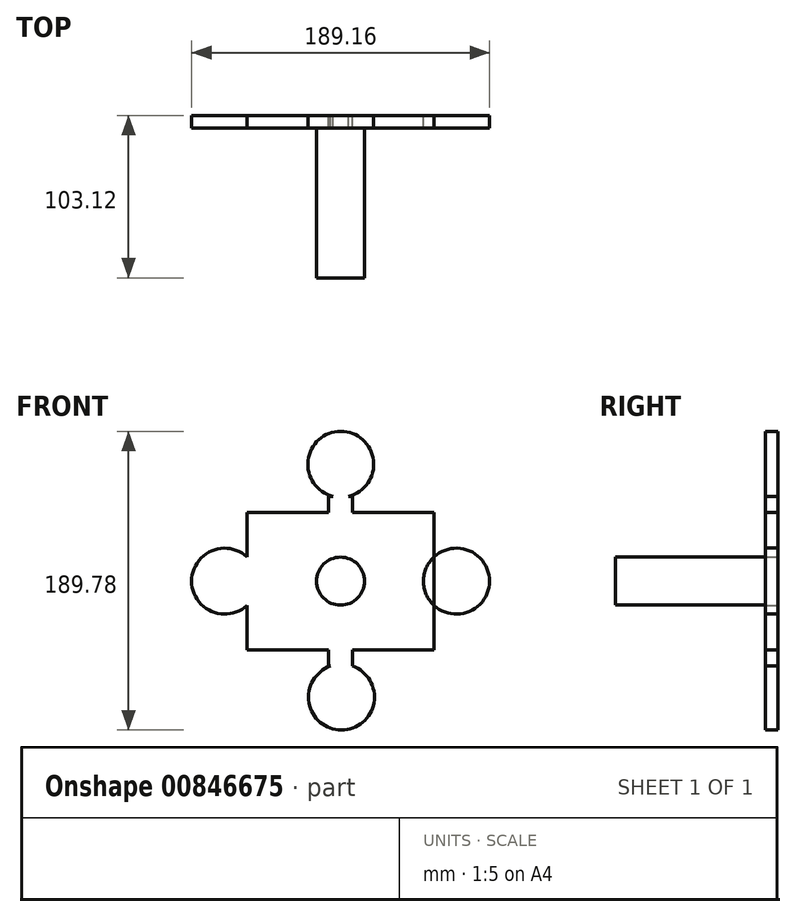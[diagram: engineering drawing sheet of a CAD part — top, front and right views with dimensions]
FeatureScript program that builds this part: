
annotation { "Feature Type Name" : "Feature", "Feature Type Description" : "" }
export const myFeature = defineFeature(function(context is Context, id is Id, definition is map)
    precondition{}
    {
        {
            var Q0;
            Q0=qCreatedBy(makeId("Front.planeOp"),FACE);
            var sketch = newSketch(context, id + "F0", { "sketchPlane" : qUnion([Q0])});
            skCircle(sketch, "E0", {"center": v(0, 0) * mm, "radius": 73.64 * mm, "construction": true});
            skCircle(sketch, "E1", {"center": v(-73.64, 0) * mm, "radius": 20.94 * mm});
            skCircle(sketch, "E2.MirrorC", {"center": v(73.64, 0) * mm, "radius": 20.94 * mm});
            skCircle(sketch, "E3", {"center": v(0.12, 74.26) * mm, "radius": 20.94 * mm});
            skCircle(sketch, "E4", {"center": v(0.6, -73.64) * mm, "radius": 20.94 * mm});
            skLineSegment(sketch, "E5.bottom", {"start": v(7.57, -53.9) * mm, "end": v(-7.57, -53.9) * mm});
            skLineSegment(sketch, "E5.top", {"start": v(7.57, 53.9) * mm, "end": v(-7.57, 53.9) * mm});
            skLineSegment(sketch, "E5.left", {"start": v(7.57, -53.9) * mm, "end": v(7.57, 53.9) * mm});
            skLineSegment(sketch, "E5.right", {"start": v(-7.57, -53.9) * mm, "end": v(-7.57, 53.9) * mm});
            skLineSegment(sketch, "E6.bottom", {"start": v(59.32, -43.64) * mm, "end": v(-59.32, -43.64) * mm});
            skLineSegment(sketch, "E6.top", {"start": v(59.32, 43.64) * mm, "end": v(-59.32, 43.64) * mm});
            skLineSegment(sketch, "E6.left", {"start": v(59.32, -43.64) * mm, "end": v(59.32, 43.64) * mm});
            skLineSegment(sketch, "E6.right", {"start": v(-59.32, -43.64) * mm, "end": v(-59.32, 43.64) * mm});
            skSolve(sketch);
        }
        {
            var Q0;
            {var subQ0=sQuery(id+"F0.wireOp",EDGE,"E5.top");var subQ1=sQuery(id+"F0.wireOp",EDGE,"E3");var subQ2=makeQuery(id+"F0.imprint","INTERSECT",VERTEX,{"disambiguationData":[OD(0.0)],"derivedFrom":[subQ1,subQ0]});Q0=makeQuery(id+"F0.imprint","IMPRINT",FACE,{"disambiguationData":[TD([[makeQuery(id+"F0.imprint","IMPRINT",EDGE,{"disambiguationData":[TD([[subQ2,-1.0]])],"derivedFrom":subQ1}),1.0]])]});}
            var Q1;
            {var subQ0=sQuery(id+"F0.wireOp",EDGE,"E6.right");var subQ8=sQuery(id+"F0.wireOp",EDGE,"E1");var subQ9=makeQuery(id+"F0.imprint","INTERSECT",VERTEX,{"disambiguationData":[OD(0.0)],"derivedFrom":[subQ8,subQ0]});Q1=makeQuery(id+"F0.imprint","IMPRINT",FACE,{"disambiguationData":[TD([[makeQuery(id+"F0.imprint","IMPRINT",EDGE,{"disambiguationData":[TD([[subQ9,-1.0]])],"derivedFrom":subQ8}),-1.0]])]});}
            var Q2;
            {var subQ0=sQuery(id+"F0.wireOp",EDGE,"E6.bottom");var subQ1=sQuery(id+"F0.wireOp",EDGE,"E5.left");var subQ2=makeQuery(id+"F0.imprint","INTERSECT",VERTEX,{"derivedFrom":[subQ1,subQ0]});Q2=makeQuery(id+"F0.imprint","IMPRINT",FACE,{"disambiguationData":[TD([[makeQuery(id+"F0.imprint","IMPRINT",EDGE,{"disambiguationData":[TD([[subQ2,-1.0]])],"derivedFrom":subQ1}),1.0]])]});}
            var Q3;
            {var subQ0=sQuery(id+"F0.wireOp",EDGE,"E6.left");var subQ8=sQuery(id+"F0.wireOp",EDGE,"E2.MirrorC");var subQ9=makeQuery(id+"F0.imprint","INTERSECT",VERTEX,{"disambiguationData":[OD(0.0)],"derivedFrom":[subQ8,subQ0]});Q3=makeQuery(id+"F0.imprint","IMPRINT",FACE,{"disambiguationData":[TD([[makeQuery(id+"F0.imprint","IMPRINT",EDGE,{"disambiguationData":[TD([[subQ9,-1.0]])],"derivedFrom":subQ8}),1.0]])]});}
            var Q4;
            {var subQ1=sQuery(id+"F0.wireOp",EDGE,"E5.top");var subQ3=sQuery(id+"F0.wireOp",EDGE,"E3");var subQ10=makeQuery(id+"F0.imprint","INTERSECT",VERTEX,{"disambiguationData":[OD(0.0)],"derivedFrom":[subQ3,subQ1]});Q4=makeQuery(id+"F0.imprint","IMPRINT",FACE,{"disambiguationData":[TD([[makeQuery(id+"F0.imprint","IMPRINT",EDGE,{"disambiguationData":[TD([[subQ10,1.0]])],"derivedFrom":subQ3}),-1.0]])]});}
            var Q5;
            {var subQ0=sQuery(id+"F0.wireOp",EDGE,"E6.left");var subQ1=sQuery(id+"F0.wireOp",EDGE,"E2.MirrorC");var subQ2=makeQuery(id+"F0.imprint","INTERSECT",VERTEX,{"disambiguationData":[OD(0.0)],"derivedFrom":[subQ1,subQ0]});Q5=makeQuery(id+"F0.imprint","IMPRINT",FACE,{"disambiguationData":[TD([[makeQuery(id+"F0.imprint","IMPRINT",EDGE,{"disambiguationData":[TD([[subQ2,-1.0]])],"derivedFrom":subQ1}),-1.0]])]});}
            var Q6;
            {var subQ0=sQuery(id+"F0.wireOp",EDGE,"E6.right");var subQ1=sQuery(id+"F0.wireOp",EDGE,"E1");var subQ2=makeQuery(id+"F0.imprint","INTERSECT",VERTEX,{"disambiguationData":[OD(0.0)],"derivedFrom":[subQ1,subQ0]});Q6=makeQuery(id+"F0.imprint","IMPRINT",FACE,{"disambiguationData":[TD([[makeQuery(id+"F0.imprint","IMPRINT",EDGE,{"disambiguationData":[TD([[subQ2,1.0]])],"derivedFrom":subQ1}),1.0]])]});}
            var Q7;
            {var subQ0=sQuery(id+"F0.wireOp",EDGE,"E6.right");var subQ1=sQuery(id+"F0.wireOp",EDGE,"E1");var subQ2=makeQuery(id+"F0.imprint","INTERSECT",VERTEX,{"disambiguationData":[OD(0.0)],"derivedFrom":[subQ1,subQ0]});Q7=makeQuery(id+"F0.imprint","IMPRINT",FACE,{"disambiguationData":[TD([[makeQuery(id+"F0.imprint","IMPRINT",EDGE,{"disambiguationData":[TD([[subQ2,-1.0]])],"derivedFrom":subQ1}),1.0]])]});}
            var Q8;
            {var subQ0=sQuery(id+"F0.wireOp",EDGE,"E5.bottom");var subQ1=sQuery(id+"F0.wireOp",EDGE,"E4");var subQ3=makeQuery(id+"F0.imprint","INTERSECT",VERTEX,{"derivedFrom":[subQ1,subQ0]});Q8=makeQuery(id+"F0.imprint","IMPRINT",FACE,{"disambiguationData":[TD([[makeQuery(id+"F0.imprint","IMPRINT",EDGE,{"disambiguationData":[TD([[subQ3,-1.0]])],"derivedFrom":subQ1}),1.0]])]});}
            var Q9;
            {var subQ1=sQuery(id+"F0.wireOp",EDGE,"E5.bottom");var subQ6=sQuery(id+"F0.wireOp",EDGE,"E5.right");var subQ7=makeQuery(id+"F0.imprint","INTERSECT",VERTEX,{"derivedFrom":[subQ1,subQ6]});Q9=makeQuery(id+"F0.imprint","IMPRINT",FACE,{"disambiguationData":[TD([[makeQuery(id+"F0.imprint","IMPRINT",EDGE,{"disambiguationData":[TD([[subQ7,1.0]])],"derivedFrom":subQ1}),-1.0]])]});}
            var Q10;
            {var subQ0=sQuery(id+"F0.wireOp",EDGE,"E6.left");var subQ1=sQuery(id+"F0.wireOp",EDGE,"E2.MirrorC");var subQ2=makeQuery(id+"F0.imprint","INTERSECT",VERTEX,{"disambiguationData":[OD(0.0)],"derivedFrom":[subQ1,subQ0]});Q10=makeQuery(id+"F0.imprint","IMPRINT",FACE,{"disambiguationData":[TD([[makeQuery(id+"F0.imprint","IMPRINT",EDGE,{"disambiguationData":[TD([[subQ2,1.0]])],"derivedFrom":subQ1}),-1.0]])]});}
            var Q11;
            {var subQ0=sQuery(id+"F0.wireOp",EDGE,"E5.bottom");var subQ1=sQuery(id+"F0.wireOp",EDGE,"E4");var subQ3=makeQuery(id+"F0.imprint","INTERSECT",VERTEX,{"derivedFrom":[subQ1,subQ0]});Q11=makeQuery(id+"F0.imprint","IMPRINT",FACE,{"disambiguationData":[TD([[makeQuery(id+"F0.imprint","IMPRINT",EDGE,{"disambiguationData":[TD([[subQ3,1.0]])],"derivedFrom":subQ1}),1.0]])]});}
            var Q12;
            {var subQ0=sQuery(id+"F0.wireOp",EDGE,"E5.top");var subQ1=sQuery(id+"F0.wireOp",EDGE,"E3");var subQ2=makeQuery(id+"F0.imprint","INTERSECT",VERTEX,{"disambiguationData":[OD(0.0)],"derivedFrom":[subQ1,subQ0]});Q12=makeQuery(id+"F0.imprint","IMPRINT",FACE,{"disambiguationData":[TD([[makeQuery(id+"F0.imprint","IMPRINT",EDGE,{"disambiguationData":[TD([[subQ2,1.0]])],"derivedFrom":subQ1}),1.0]])]});}
            extrude(context, id + "F1", {"entities" : qUnion([Q0, Q1, Q2, Q3, Q4, Q5, Q6, Q7, Q8, Q9, Q10, Q11, Q12]), "depth" : 8 * mm, "offsetDistance" : 25.4 * mm});
        }
        {
            var Q0;
            Q0=qCreatedBy(makeId("Front.planeOp"),FACE);
            var sketch = newSketch(context, id + "F2", { "sketchPlane" : qUnion([Q0])});
            skCircle(sketch, "E7", {"center": v(0, 0) * mm, "radius": 15.24 * mm});
            skSolve(sketch);
        }
        {
            var Q0;
            Q0 = qSketchRegion(id + "F2", true);
            extrude(context, id + "F3", {"entities" : qUnion([Q0]), "operationType" : NewBodyOperationType.ADD, "depth" : 103.12 * mm, "offsetDistance" : 25.4 * mm});
        }
    });
